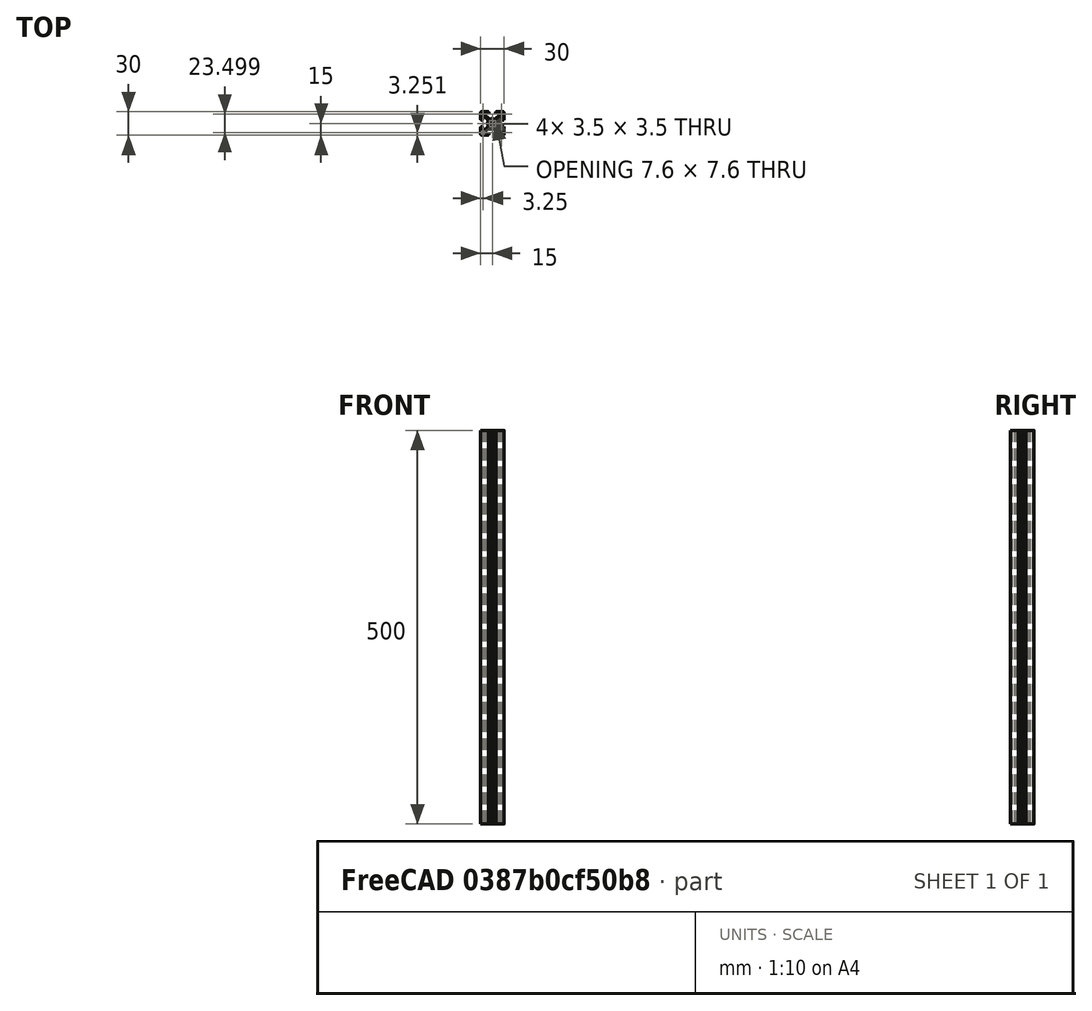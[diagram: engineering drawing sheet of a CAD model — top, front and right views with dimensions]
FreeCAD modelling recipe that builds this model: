
FCSTD DOCUMENT  (FreeCAD 0.21R33771 (Git))
Label: aluminiumProfile
License: All rights reserved
LicenseURL: http://en.wikipedia.org/wiki/All_rights_reserved
objects: Part::Feature×1, Sketcher::SketchObject×1, PartDesign::FeatureBase×1, PartDesign::Pocket×1, PartDesign::Body×1
note: 6 computed .brp shape members not serialized (recipe doc carries the construction recipe); baked Part::Feature solids carry a one-line shape summary decoded from their .brp

FEATURE [Part::Feature] Part__Feature  label="30x30profile"
  shape: bbox 30 x 30 x 1000 mm, 123 faces (baked)
FEATURE [Sketcher::SketchObject] Sketch
  FullyConstrained = false
  MapMode = 5
  Placement = pos=(0,0,1000) rot=(0,0,1;0rad)
  Support = -> [Part__Feature]
  sketch-geometry (1):
    g0: Circle CenterX=0 CenterY=0 CenterZ=0 NormalX=0 NormalY=0 NormalZ=1 AngleXU=0 Radius=24.6835
  constraints (1):
    c: Coincident(g0,g-1)
FEATURE [PartDesign::FeatureBase] BaseFeature
  BaseFeature = -> Part__Feature
FEATURE [PartDesign::Pocket] Pocket
  BaseFeature = -> BaseFeature
  Direction = (0,0,-1)
  Length = 500
  Length2 = 5
  Profile = -> Sketch
  ReferenceAxis = -> Sketch [N_Axis]
  Refine = true
  Type = 0
FEATURE [PartDesign::Body] Body
  BaseFeature = -> Part__Feature
  Group = -> [BaseFeature,Sketch,Pocket]
  Origin = -> Origin
  Tip = -> Pocket
